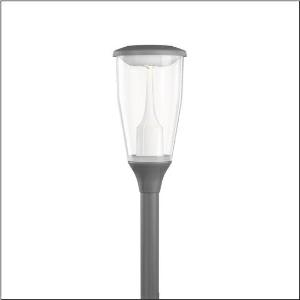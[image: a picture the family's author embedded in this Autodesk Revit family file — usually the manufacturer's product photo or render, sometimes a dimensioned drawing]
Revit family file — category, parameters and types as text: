
# Revit family: dl_11_iq___p1_0a_5xa5575bf14hp00022_48d3
name_source: partatom
category: Lighting Fixtures
units: mm (PartAtom-declared; Revit-internal decimal feet)

## family parameters
Cut with Voids When Loaded = No
Host = Face
Light Source = No
Part Type = Normal
Room Calculation Point = No
Round Connector Dimension = Use Diameter
Shared = No

## types (1)
- --- (1 x LED, 3950 lm, 33.6 W, 2200K)
    Apparent Load = 34 VA
    CIE Flux Codes = 33 63 91 94 100
    Color Rendering = 70
    Color Temperature = 2200K
    Default Elevation = 1800 mm
    Description = DL 11 iQ, mast luminaire, Module 540 iQ-SR, primary light control with 3 zone facetted reflector, of plastic, silver coated, highly specular, structured, primary optical cover: cover, of PMMA, transparent, light distribution: P1.0a, light emission: direct distribution, primary light characteristic: asymmetric, installation type: post-top, LED, High Power LED, light colour: 722, colour temperature: 2200K, control gear: iQ Street-Remote, control: Street-Remote, Auto-Match, Temp-Guard, Lumen-Switch, Night-Set, Smart-Wire, Light-Fading, Desk-Remote (wireless, voltage-free reading and setting of iQ features in the workshop via application-optimized NFC function/RFID function), optimised constant luminous flux control (CLO 2.0), mains connection: 220..240V, AC, 50/60Hz, connection cable pre-assembled, cable length: 5,5m, wiring characteristics: H07RN-F, 5-core, 1.5mm², start of lifetime: 34W, end of service life: 36W, luminaire housing, upper part, of diecast aluminium, coated, SITECO metallic grey (DB 702S), spigot size: 76mm (post-top), mounting height: 3..5m, post-top mast mounting element, of diecast aluminium, coated, SITECO metallic grey (DB 702S), Module 540 iQ-SR, traffic white (RAL 9016), equipment: Power, protection rating (complete): IP66, insulation class (complete): insulation class II (safety insulation), certification: CE, ENEC, ENEC+, VDE, impact resistance: IK07, packaging unit: 1 piece

Light Distribution: P1.0a
    Height = 665 mm
    Lamp = 1 x LED
    Lamp Light Flux = 3950 lm
    Lamp Power = 33.6 W
    Lamp count = 1
    Length = 334 mm
    Luminous efficacy = 118 lm/W
    Manufacturer = Siteco
    ModVariant = No
    Model = 5XA5575BF14HP00022
    Mounting Place = Pole
    Mounting Type = Pole top
    Number of Poles = 1
    OnlyDefault = Yes
    Power Factor = 1
    Product Name = DL 11 iQ | P1.0a
    Product group = mast luminaire | pylon top
    ProductGroupID = 6100
    Protection Class = Protection class II
    Protection Degree = IP 66
    RLX_Detail_Level = 1
    RLX_Emergency_Light_Flux = 0 lm
    RLX_Emergency_Type = 0
    RLX_Emergency_Type_DB = No
    RlxData = <blob elided: 104261 chars, md5=52518e0c>
    Socket = socket
    Standby Power = 0 W
    System Light Flux = 3950 lm
    System Power = 34 W
    Type Comments = factory setting: luminous flux: 100 % | dim-lin: 254 | 695 mA
    Type Image = l_1258354.jpg
    URL = http://relux.com
    VarID = @adj_041455
    Voltage = 0 V
    Weight = 0.00 kg
    Width = 0 mm  [stored 0 ft]

note: [stored X ft] marks values corroborated as IEEE doubles in the binary element streams (Revit-internal decimal feet)

## geometry (parser evidence)
native form markers: Blend x4, Sweep x11
no freeform markers — native parametric forms only
